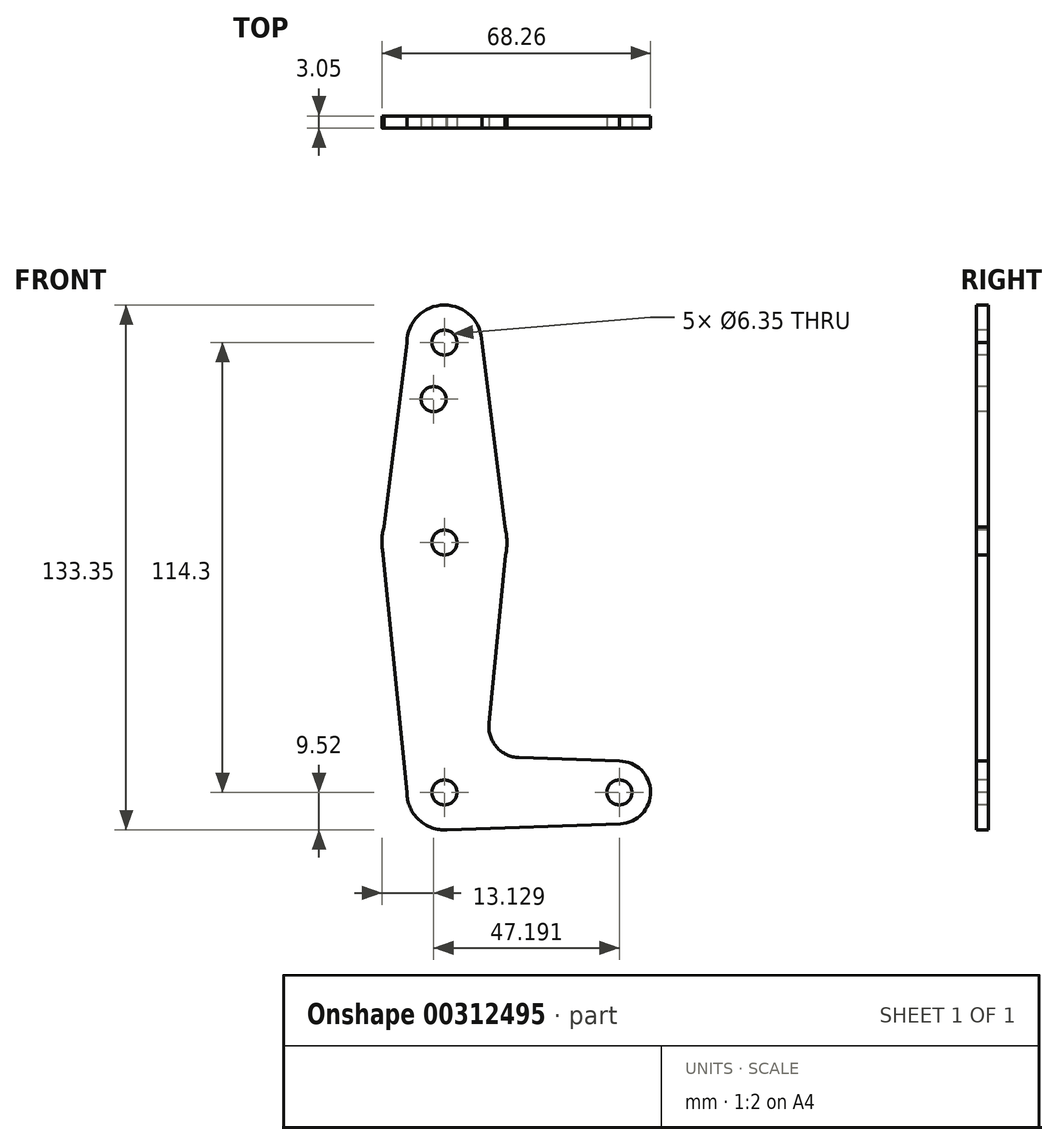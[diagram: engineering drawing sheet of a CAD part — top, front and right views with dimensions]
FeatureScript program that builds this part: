
annotation { "Feature Type Name" : "Feature", "Feature Type Description" : "" }
export const myFeature = defineFeature(function(context is Context, id is Id, definition is map)
    precondition{}
    {
        {
            var Q0;
            Q0=qCreatedBy(makeId("Front.planeOp"),FACE);
            var sketch = newSketch(context, id + "F0", { "sketchPlane" : qUnion([Q0])});
            skLineSegment(sketch, "E0", {"start": v(-55.67, 59.68) * mm, "end": v(-55.67, -54.62) * mm, "construction": true});
            skLineSegment(sketch, "E1", {"start": v(-55.67, -54.62) * mm, "end": v(-11.22, -54.62) * mm, "construction": true});
            skCircle(sketch, "E2", {"center": v(-55.67, 59.68) * mm, "radius": 9.53 * mm});
            skCircle(sketch, "E3", {"center": v(-55.67, 8.88) * mm, "radius": 15.88 * mm});
            skCircle(sketch, "E4", {"center": v(-55.67, -54.62) * mm, "radius": 9.53 * mm});
            skCircle(sketch, "E5", {"center": v(-11.22, -54.62) * mm, "radius": 7.94 * mm});
            skLineSegment(sketch, "E6", {"start": v(-65.2, 59.68) * mm, "end": v(-71.54, 8.88) * mm});
            skLineSegment(sketch, "E7", {"start": v(-46.14, 59.68) * mm, "end": v(-39.8, 8.88) * mm});
            skLineSegment(sketch, "E8", {"start": v(-71.54, 8.88) * mm, "end": v(-65.2, -54.62) * mm});
            skLineSegment(sketch, "E9", {"start": v(-39.8, 8.88) * mm, "end": v(-44.35, -37.04) * mm});
            skLineSegment(sketch, "E10", {"start": v(-36.72, -45.77) * mm, "end": v(-11.22, -46.68) * mm});
            skLineSegment(sketch, "E11", {"start": v(-55.67, -64.14) * mm, "end": v(-10.94, -62.56) * mm});
            skCircle(sketch, "E12", {"center": v(-55.67, 59.68) * mm, "radius": 3.18 * mm});
            skCircle(sketch, "E13", {"center": v(-55.67, 8.88) * mm, "radius": 3.18 * mm});
            skCircle(sketch, "E14", {"center": v(-11.22, -54.62) * mm, "radius": 3.18 * mm});
            skCircle(sketch, "E15", {"center": v(-58.41, 45.3) * mm, "radius": 3.18 * mm});
            skLineSegment(sketch, "E16", {"start": v(-58.41, 45.3) * mm, "end": v(-58.17, 42.14) * mm});
            skLineSegment(sketch, "E17.trimOffspring", {"start": v(-55.9, 12.05) * mm, "end": v(-55.67, 8.88) * mm});
            skCircle(sketch, "E18", {"center": v(-55.67, -54.62) * mm, "radius": 3.18 * mm});
            skPoint(sketch, "E19.newPointA", {"position": v(-46.1, -54.62) * mm});
            skArc(sketch, "E19.filletArc", {"start": v(-44.35, -37.04) * mm, "mid": v(-42.43, -43.06) * mm, "end": v(-36.72, -45.77) * mm});
            skSolve(sketch);
        }
        {
            var Q0;
            Q0 = qSketchRegion(id + "F0", true);
            var Q1;
            Q1=makeQuery(id+"F0.imprint","IMPRINT",FACE,{"disambiguationData":[TD([[makeQuery(id+"F0.imprint","IMPRINT",EDGE,{"derivedFrom":sQuery(id+"F0.wireOp",EDGE,"E15")}),-1.0]])]});
            extrude(context, id + "F1", {"entities" : qUnion([Q0, Q1]), "oppositeDirection" : true, "depth" : 3.05 * mm});
        }
    });
